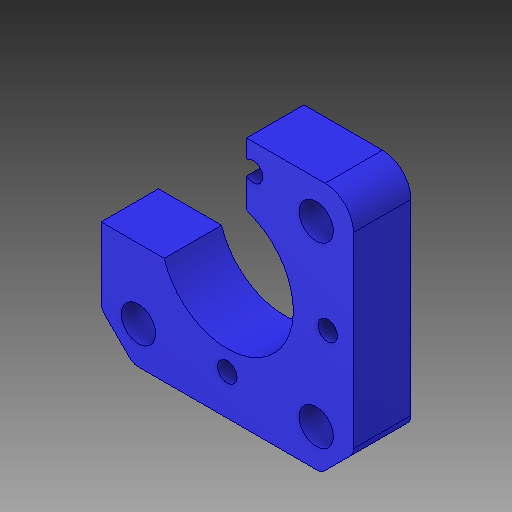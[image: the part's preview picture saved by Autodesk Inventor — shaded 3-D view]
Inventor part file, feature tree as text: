
AUTODESK INVENTOR PART (.ipt)
format: ipt  version: 2019 (Build 230136000, 136)  size: 366,592 bytes
history: native  units: mm
features: thicken_offset x1, fillet x1
ambient origin geometry x8: Origin, YZ Plane, XZ Plane, XY Plane, X Axis, Y Axis, Z Axis, Center Point
bodies: Solid1 (feature_tree)
feature tree (2):
  thicken_offset  "Thicken1"
  fillet  "Fillet1"  Radius=1.0mm
